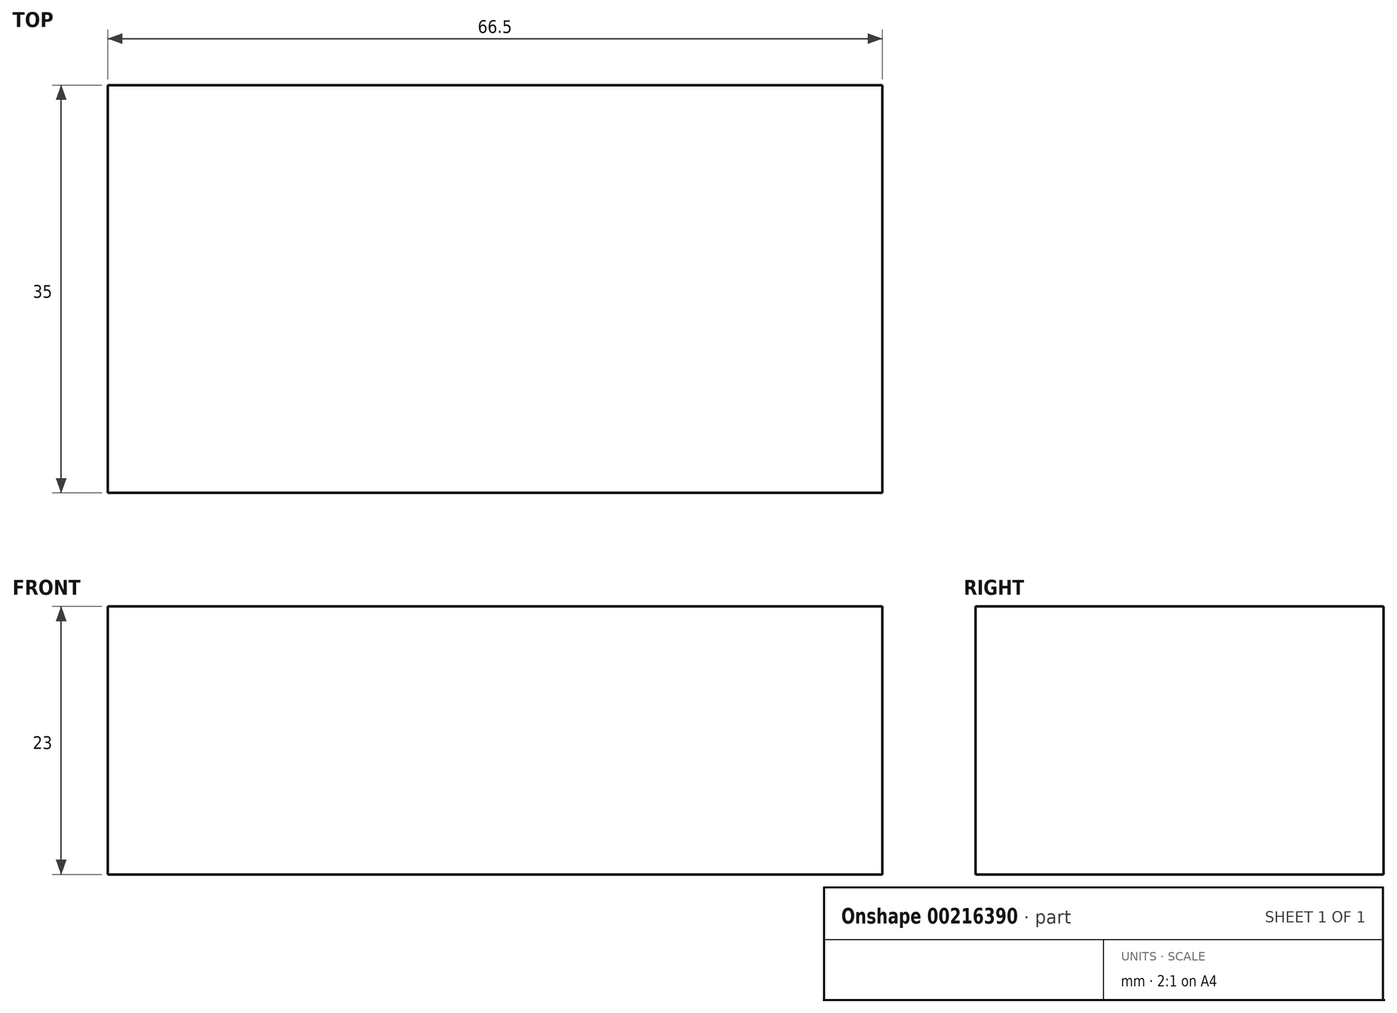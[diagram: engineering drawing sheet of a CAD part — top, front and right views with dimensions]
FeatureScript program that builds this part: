
annotation { "Feature Type Name" : "Feature", "Feature Type Description" : "" }
export const myFeature = defineFeature(function(context is Context, id is Id, definition is map)
    precondition{}
    {
        {
            var Q0;
            Q0=qCreatedBy(makeId("Top.planeOp"),FACE);
            var sketch = newSketch(context, id + "F0", { "sketchPlane" : qUnion([Q0])});
            skLineSegment(sketch, "E0.bottom", {"start": v(33.25, -17.5) * mm, "end": v(-33.25, -17.5) * mm});
            skLineSegment(sketch, "E0.top", {"start": v(33.25, 17.5) * mm, "end": v(-33.25, 17.5) * mm});
            skLineSegment(sketch, "E0.left", {"start": v(33.25, -17.5) * mm, "end": v(33.25, 17.5) * mm});
            skLineSegment(sketch, "E0.right", {"start": v(-33.25, -17.5) * mm, "end": v(-33.25, 17.5) * mm});
            skPoint(sketch, "E0.middle", {"position": v(0, 0) * mm});
            skSolve(sketch);
        }
        {
            var Q0;
            Q0=qSketchRegion(id+"F0",true);
            extrude(context, id + "F1", {"entities" : qUnion([Q0]), "depth" : 23 * mm});
        }
    });
